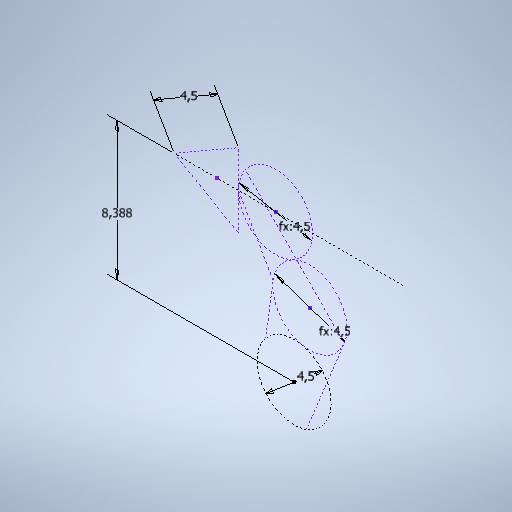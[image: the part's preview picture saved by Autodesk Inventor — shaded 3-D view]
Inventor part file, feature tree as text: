
AUTODESK INVENTOR PART (.ipt)
format: ipt  version: 2025.2 (Build 292293000, 293)  size: 262,144 bytes
history: native  units: mm
features: sketch x1
ambient origin geometry x8: Origin, YZ Plane, XZ Plane, XY Plane, X Axis, Y Axis, Z Axis, Center Point
feature tree (1):
  sketch  "Esboço1"  dims[d0=4.5mm d1=4.5mm d2=4.5mm d3=4.5mm d4=8.387539mm]
